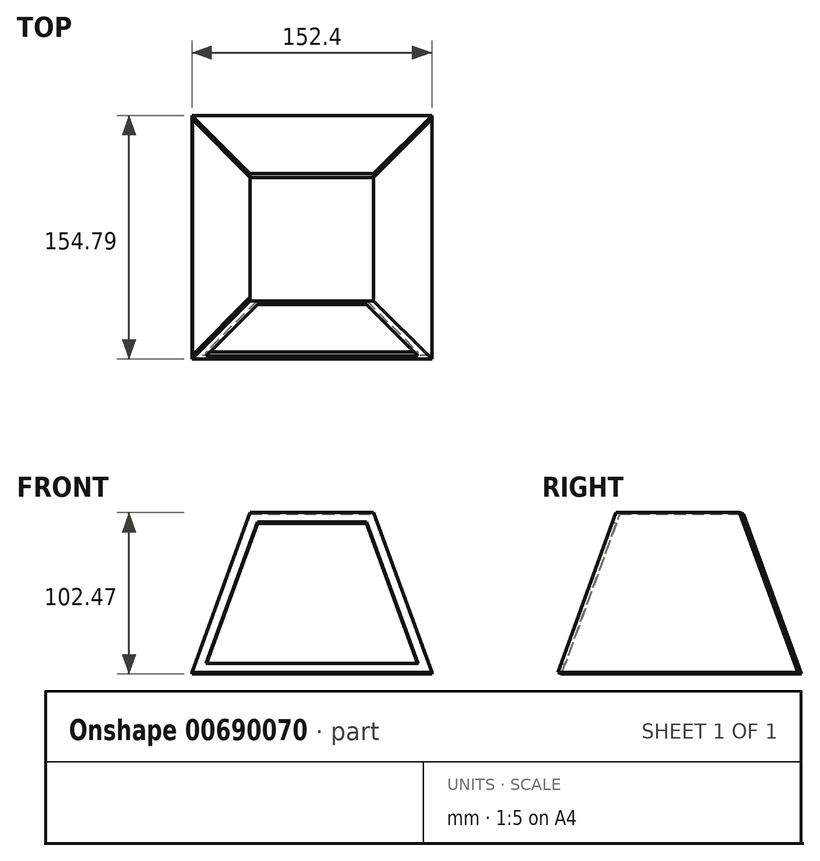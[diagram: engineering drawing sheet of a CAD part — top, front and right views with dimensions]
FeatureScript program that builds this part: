
annotation { "Feature Type Name" : "Feature", "Feature Type Description" : "" }
export const myFeature = defineFeature(function(context is Context, id is Id, definition is map)
    precondition{}
    {
        {
            var Q0;
            Q0=qCreatedBy(makeId("Top.planeOp"),FACE);
            var sketch = newSketch(context, id + "F0", { "sketchPlane" : qUnion([Q0])});
            skLineSegment(sketch, "E0.bottom", {"start": v(76.2, 76.2) * mm, "end": v(-76.2, 76.2) * mm});
            skLineSegment(sketch, "E0.top", {"start": v(76.2, -76.2) * mm, "end": v(-76.2, -76.2) * mm});
            skLineSegment(sketch, "E0.left", {"start": v(76.2, 76.2) * mm, "end": v(76.2, -76.2) * mm});
            skLineSegment(sketch, "E0.right", {"start": v(-76.2, 76.2) * mm, "end": v(-76.2, -76.2) * mm});
            skPoint(sketch, "E0.middle", {"position": v(0, 0) * mm});
            skSolve(sketch);
        }
        {
            var Q0;
            Q0 = qSketchRegion(id + "F0", true);
            extrude(context, id + "F1", {"entities" : qUnion([Q0]), "depth" : 101.6 * mm, "offsetDistance" : 25.4 * mm, "hasDraft" : true, "draftAngle" : 20 * degree, "draftPullDirection" : true});
        }
        {
            var Q0;
            Q0=makeQuery(id+"F1.opExtrude","SWEPT_FACE",FACE,{"disambiguationData":[OSD([sQuery(id+"F0.wireOp",EDGE,"E0.top")])]});
            var sketch = newSketch(context, id + "F2", { "sketchPlane" : qUnion([Q0])});
            skLineSegment(sketch, "E1.0", {"start": v(-39.22, 82.06) * mm, "end": v(-76.2, -26.06) * mm});
            skLineSegment(sketch, "E2.0", {"start": v(39.22, 82.06) * mm, "end": v(-39.22, 82.06) * mm});
            skLineSegment(sketch, "E3.0", {"start": v(39.22, 82.06) * mm, "end": v(76.2, -26.06) * mm});
            skLineSegment(sketch, "E4.0", {"start": v(76.2, -26.06) * mm, "end": v(-76.2, -26.06) * mm});
            skLineSegment(sketch, "E5.0", {"start": v(-34.68, 75.7) * mm, "end": v(-67.32, -19.71) * mm});
            skLineSegment(sketch, "E5.1", {"start": v(34.68, 75.7) * mm, "end": v(-34.68, 75.7) * mm});
            skLineSegment(sketch, "E5.2", {"start": v(34.68, 75.7) * mm, "end": v(67.32, -19.71) * mm});
            skLineSegment(sketch, "E5.3", {"start": v(67.32, -19.71) * mm, "end": v(-67.32, -19.71) * mm});
            skSolve(sketch);
        }
        {
            var Q0;
            Q0=makeQuery(id+"F2.imprint","IMPRINT",FACE,{"disambiguationData":[TD([[makeQuery(id+"F2.imprint","IMPRINT",EDGE,{"derivedFrom":sQuery(id+"F2.wireOp",EDGE,"E1.0")}),1.0]])]});
            var Q1;
            Q1=makeQuery(id+"F1.opExtrude","CAP_FACE",FACE,{"disambiguationData":[OSD([sQuery(id+"F0.wireOp",EDGE,"E0.bottom"),sQuery(id+"F0.wireOp",EDGE,"E0.top"),sQuery(id+"F0.wireOp",EDGE,"E0.left"),sQuery(id+"F0.wireOp",EDGE,"E0.right")])],"isStart":true});
            var Q2;
            Q2=makeQuery(id+"F1.opExtrude","CAP_FACE",FACE,{"disambiguationData":[OSD([sQuery(id+"F0.wireOp",EDGE,"E0.bottom"),sQuery(id+"F0.wireOp",EDGE,"E0.top"),sQuery(id+"F0.wireOp",EDGE,"E0.left"),sQuery(id+"F0.wireOp",EDGE,"E0.right")])],"isStart":false});
            var Q3;
            Q3=makeQuery(id+"F1.opExtrude","SWEPT_FACE",FACE,{"disambiguationData":[OSD([sQuery(id+"F0.wireOp",EDGE,"E0.bottom")])]});
            var Q4;
            Q4=makeQuery(id+"F1.opExtrude","SWEPT_FACE",FACE,{"disambiguationData":[OSD([sQuery(id+"F0.wireOp",EDGE,"E0.left")])]});
            extrude(context, id + "F3", {"entities" : qUnion([Q0, Q1, Q2, Q3, Q4]), "operationType" : NewBodyOperationType.ADD, "depth" : 2.54 * mm, "offsetDistance" : 25.4 * mm});
        }
    });
